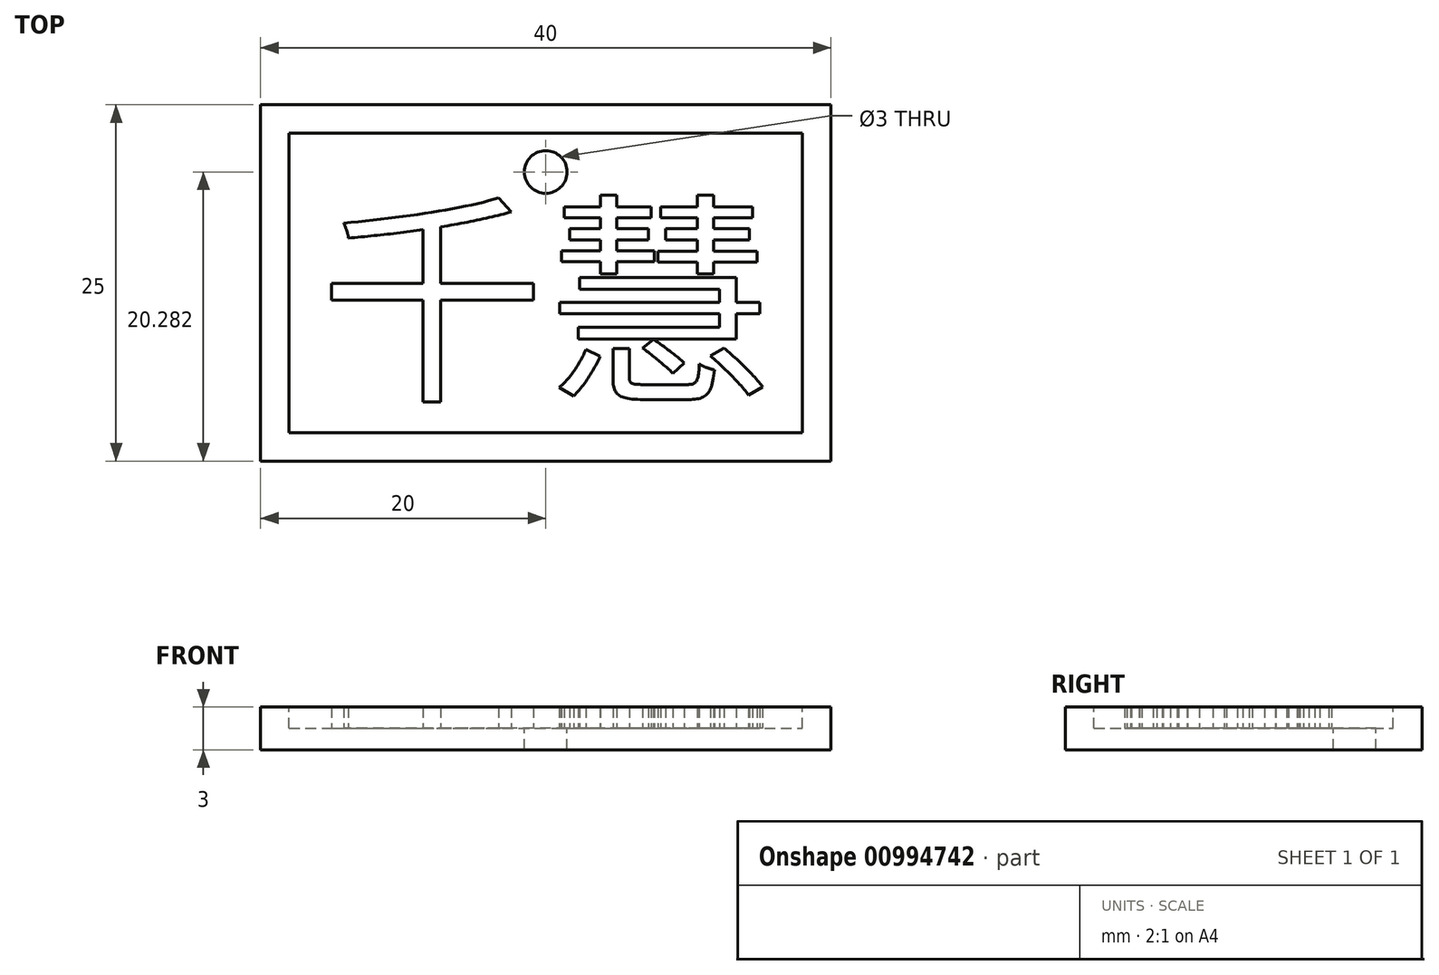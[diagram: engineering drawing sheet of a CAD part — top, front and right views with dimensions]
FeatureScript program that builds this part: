
annotation { "Feature Type Name" : "Feature", "Feature Type Description" : "" }
export const myFeature = defineFeature(function(context is Context, id is Id, definition is map)
    precondition{}
    {
        {
            var Q0;
            Q0=qCreatedBy(makeId("Top.planeOp"),FACE);
            var sketch = newSketch(context, id + "F0", { "sketchPlane" : qUnion([Q0])});
            skLineSegment(sketch, "E0.bottom", {"start": v(20, -12.5) * mm, "end": v(-20, -12.5) * mm});
            skLineSegment(sketch, "E0.top", {"start": v(20, 12.5) * mm, "end": v(-20, 12.5) * mm});
            skLineSegment(sketch, "E0.left", {"start": v(20, -12.5) * mm, "end": v(20, 12.5) * mm});
            skLineSegment(sketch, "E0.right", {"start": v(-20, -12.5) * mm, "end": v(-20, 12.5) * mm});
            skPoint(sketch, "E0.middle", {"position": v(0, 0) * mm});
            skSolve(sketch);
        }
        {
            var Q0;
            Q0 = qSketchRegion(id + "F0", true);
            extrude(context, id + "F1", {"entities" : qUnion([Q0]), "depth" : 3 * mm, "offsetDistance" : 25 * mm});
        }
        {
            var Q0;
            Q0=makeQuery(id+"F1.opExtrude","CAP_FACE",FACE,{"disambiguationData":[OSD([sQuery(id+"F0.wireOp",EDGE,"E0.bottom"),sQuery(id+"F0.wireOp",EDGE,"E0.top"),sQuery(id+"F0.wireOp",EDGE,"E0.left"),sQuery(id+"F0.wireOp",EDGE,"E0.right")])],"isStart":false});
            var sketch = newSketch(context, id + "F2", { "sketchPlane" : qUnion([Q0])});
            skLineSegment(sketch, "E1.0", {"start": v(18, -10.5) * mm, "end": v(18, 10.5) * mm});
            skLineSegment(sketch, "E1.1", {"start": v(-18, -10.5) * mm, "end": v(18, -10.5) * mm});
            skLineSegment(sketch, "E1.2", {"start": v(-18, 10.5) * mm, "end": v(-18, -10.5) * mm});
            skLineSegment(sketch, "E1.3", {"start": v(18, 10.5) * mm, "end": v(-18, 10.5) * mm});
            skSolve(sketch);
        }
        {
            var Q0;
            Q0 = qSketchRegion(id + "F2", true);
            extrude(context, id + "F3", {"entities" : qUnion([Q0]), "operationType" : NewBodyOperationType.REMOVE, "oppositeDirection" : true, "depth" : 1.5 * mm, "offsetDistance" : 25 * mm});
        }
        {
            var Q0;
            Q0=makeQuery(id+"F3.boolean.opBoolean","COPY",FACE,{"derivedFrom":makeQuery(id+"F3.opExtrude","CAP_FACE",FACE,{"disambiguationData":[OSD([sQuery(id+"F2.wireOp",EDGE,"E1.0"),sQuery(id+"F2.wireOp",EDGE,"E1.1"),sQuery(id+"F2.wireOp",EDGE,"E1.2"),sQuery(id+"F2.wireOp",EDGE,"E1.3")])],"isStart":false})});
            var sketch = newSketch(context, id + "F4", { "sketchPlane" : qUnion([Q0])});
            skCircle(sketch, "E2", {"center": v(0, 7.78) * mm, "radius": 1.5 * mm});
            skSolve(sketch);
        }
        {
            var Q0;
            Q0 = qSketchRegion(id + "F4", true);
            extrude(context, id + "F5", {"entities" : qUnion([Q0]), "operationType" : NewBodyOperationType.REMOVE, "endBound" : BoundingType.THROUGH_ALL, "oppositeDirection" : true, "depth" : 25 * mm, "offsetDistance" : 25 * mm});
        }
        {
            var Q0;
            Q0=makeQuery(id+"F3.boolean.opBoolean","COPY",FACE,{"derivedFrom":makeQuery(id+"F3.opExtrude","CAP_FACE",FACE,{"disambiguationData":[OSD([sQuery(id+"F2.wireOp",EDGE,"E1.0"),sQuery(id+"F2.wireOp",EDGE,"E1.1"),sQuery(id+"F2.wireOp",EDGE,"E1.2"),sQuery(id+"F2.wireOp",EDGE,"E1.3")])],"isStart":false})});
            var sketch = newSketch(context, id + "F6", { "sketchPlane" : qUnion([Q0])});
            skText(sketch, "E3", { "text": "千慧\n", "fontName": "NotoSansCJKtc-Regular.otf"});
            const initialGuessF6  = {"E3": [-0.0159, -0.00713, 1, 0, 0.01146]};
            skSetInitialGuess(sketch, initialGuessF6);
            skSolve(sketch);
        }
        {
            var Q0;
            Q0 = qSketchRegion(id + "F6", true);
            extrude(context, id + "F7", {"entities" : qUnion([Q0]), "operationType" : NewBodyOperationType.ADD, "depth" : 1.5 * mm, "offsetDistance" : 25 * mm});
        }
    });
